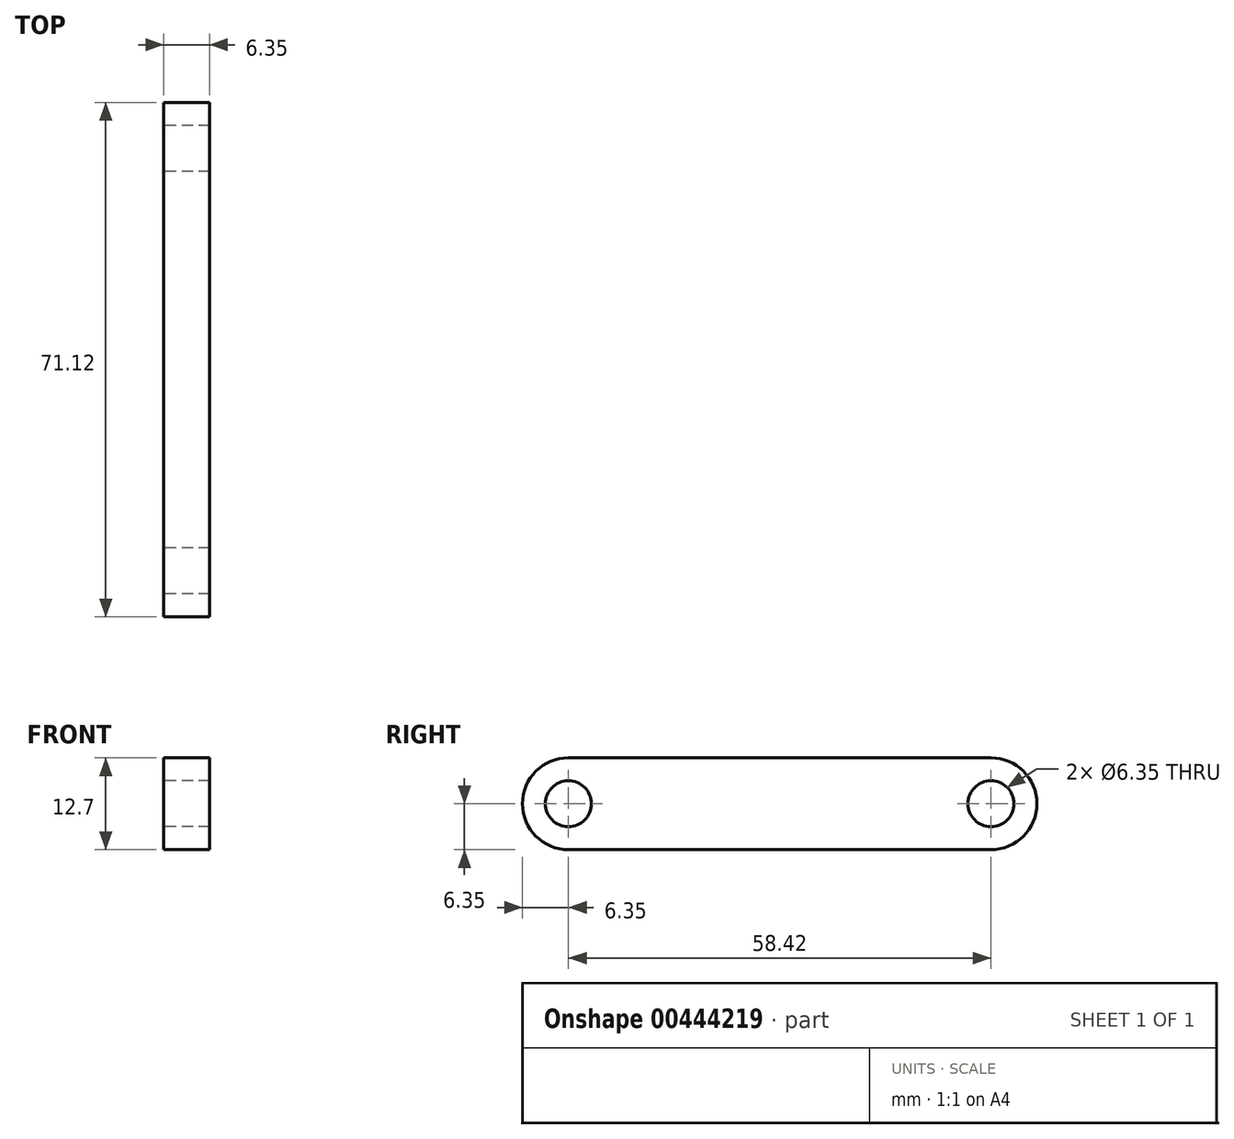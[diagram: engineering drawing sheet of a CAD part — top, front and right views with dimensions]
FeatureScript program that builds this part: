
annotation { "Feature Type Name" : "Feature", "Feature Type Description" : "" }
export const myFeature = defineFeature(function(context is Context, id is Id, definition is map)
    precondition{}
    {
        {
            var Q0;
            Q0=qCreatedBy(makeId("Right.planeOp"),FACE);
            var sketch = newSketch(context, id + "F0", { "sketchPlane" : qUnion([Q0])});
            skArc(sketch, "E0", {"start": v(-29.21, 6.35) * mm, "mid": v(-35.56, 0) * mm, "end": v(-29.21, -6.35) * mm});
            skArc(sketch, "E1", {"start": v(29.21, -6.35) * mm, "mid": v(35.56, 0) * mm, "end": v(29.21, 6.35) * mm});
            skCircle(sketch, "E2", {"center": v(29.21, 0) * mm, "radius": 3.18 * mm});
            skCircle(sketch, "E3", {"center": v(-29.21, 0) * mm, "radius": 3.18 * mm});
            skLineSegment(sketch, "E4", {"start": v(-29.21, 6.35) * mm, "end": v(29.21, 6.35) * mm});
            skLineSegment(sketch, "E5", {"start": v(-29.21, -6.35) * mm, "end": v(29.21, -6.35) * mm});
            skSolve(sketch);
        }
        {
            var Q0;
            Q0 = qSketchRegion(id + "F0", true);
            extrude(context, id + "F1", {"entities" : qUnion([Q0]), "depth" : 6.35 * mm});
        }
    });
